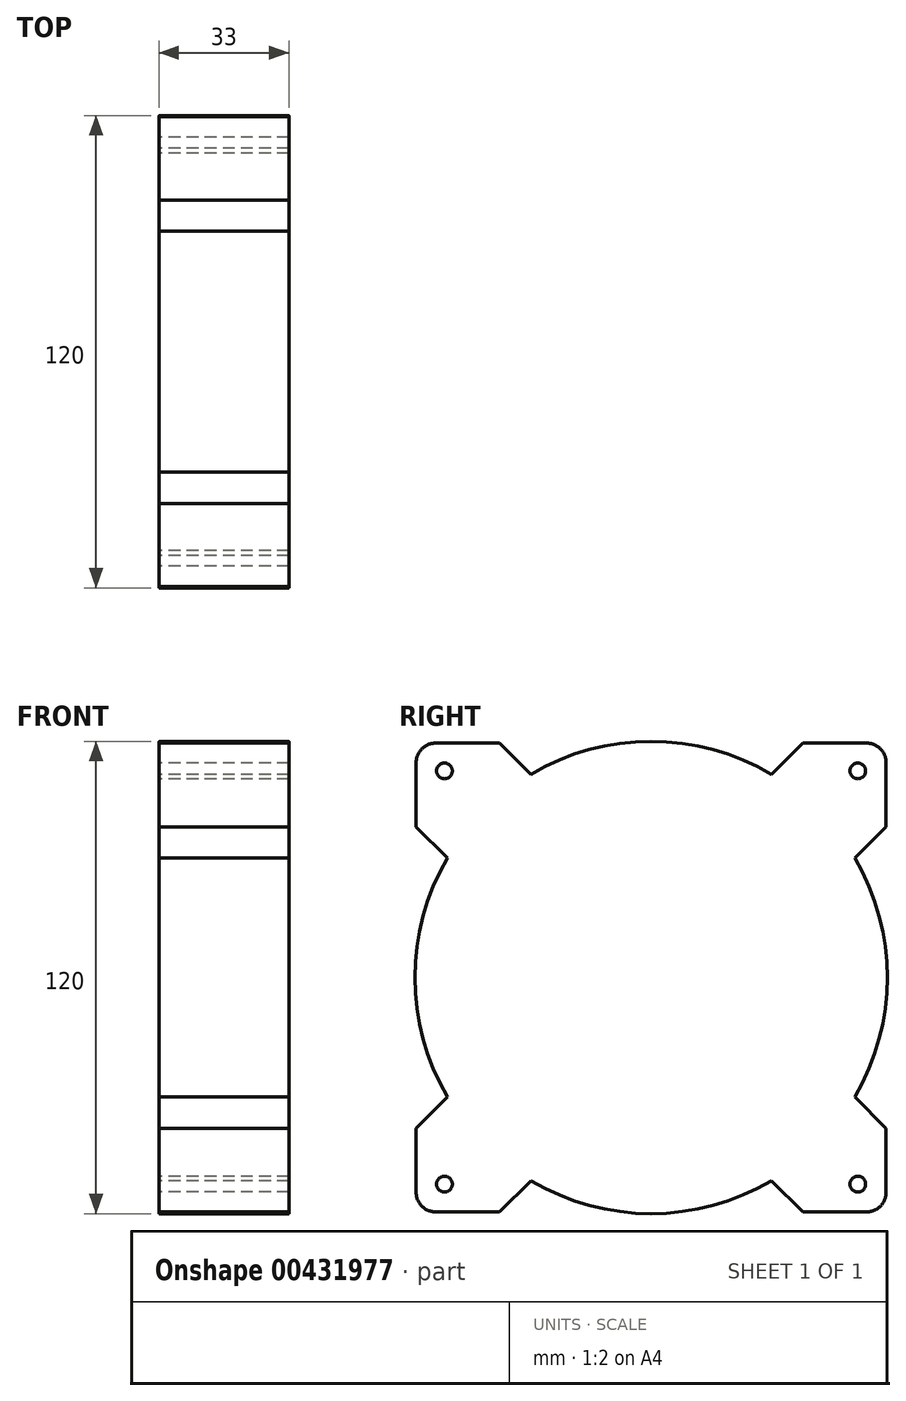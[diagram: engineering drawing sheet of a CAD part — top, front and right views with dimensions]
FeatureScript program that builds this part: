
annotation { "Feature Type Name" : "Feature", "Feature Type Description" : "" }
export const myFeature = defineFeature(function(context is Context, id is Id, definition is map)
    precondition{}
    {
        {
            var Q0;
            Q0=qCreatedBy(makeId("Right.planeOp"),FACE);
            var sketch = newSketch(context, id + "F0", { "sketchPlane" : qUnion([Q0])});
            skLineSegment(sketch, "E0.top", {"start": v(-5.3, 119.57) * mm, "end": v(-21.47, 119.57) * mm});
            skPoint(sketch, "E1.centerSnap1", {"position": v(0, 60) * mm});
            skLineSegment(sketch, "E2", {"start": v(-29.42, 111.62) * mm, "end": v(-21.47, 119.57) * mm});
            skLineSegment(sketch, "E3", {"start": v(-8.25, 90.36) * mm, "end": v(-0.3, 98.31) * mm});
            skPoint(sketch, "E4.visualSharp", {"position": v(0, 119.57) * mm});
            skArc(sketch, "E4.filletArc", {"start": v(-0.3, 114.52) * mm, "mid": v(-1.75, 118.09) * mm, "end": v(-5.3, 119.57) * mm});
            skLineSegment(sketch, "E5", {"start": v(-60, 133.31) * mm, "end": v(-60, 60) * mm, "construction": true});
            skLineSegment(sketch, "E6", {"start": v(-60, 60) * mm, "end": v(15.56, 60) * mm, "construction": true});
            skArc(sketch, "E7.trimOffspring", {"start": v(0, 60) * mm, "mid": v(-2.1, 75.73) * mm, "end": v(-8.25, 90.36) * mm});
            skLineSegment(sketch, "E8.trimOffspring", {"start": v(-0.3, 98.31) * mm, "end": v(-0.3, 114.52) * mm});
            skArc(sketch, "E9.trimOffspring", {"start": v(-29.42, 111.62) * mm, "mid": v(-44.15, 117.87) * mm, "end": v(-60, 120) * mm});
            skCircle(sketch, "E10", {"center": v(-7.5, 112.5) * mm, "radius": 2 * mm});
            skArc(sketch, "E11.MirrorCS", {"start": v(-119.7, 114.52) * mm, "mid": v(-118.25, 118.09) * mm, "end": v(-114.7, 119.57) * mm});
            skLineSegment(sketch, "E12.MirrorCS", {"start": v(-119.7, 98.31) * mm, "end": v(-119.7, 114.52) * mm});
            skArc(sketch, "E13.MirrorCS", {"start": v(-90.58, 111.62) * mm, "mid": v(-75.85, 117.87) * mm, "end": v(-60, 120) * mm});
            skCircle(sketch, "E14.MirrorC", {"center": v(-112.5, 112.5) * mm, "radius": 2 * mm});
            skPoint(sketch, "E15.MirrorP", {"position": v(-120, 119.57) * mm});
            skLineSegment(sketch, "E16.MirrorCS", {"start": v(-90.58, 111.62) * mm, "end": v(-98.53, 119.57) * mm});
            skLineSegment(sketch, "E17.MirrorCS", {"start": v(-114.7, 119.57) * mm, "end": v(-98.53, 119.57) * mm});
            skLineSegment(sketch, "E18.MirrorCS", {"start": v(-111.75, 90.36) * mm, "end": v(-119.7, 98.31) * mm});
            skArc(sketch, "E19.MirrorCS", {"start": v(-120, 60) * mm, "mid": v(-117.9, 75.73) * mm, "end": v(-111.75, 90.36) * mm});
            skArc(sketch, "E20.MirrorCS", {"start": v(-119.7, 5.48) * mm, "mid": v(-118.25, 1.91) * mm, "end": v(-114.7, 0.43) * mm});
            skArc(sketch, "E21.MirrorCS", {"start": v(-0.3, 5.48) * mm, "mid": v(-1.75, 1.91) * mm, "end": v(-5.3, 0.43) * mm});
            skLineSegment(sketch, "E22.MirrorCS", {"start": v(-111.75, 29.64) * mm, "end": v(-119.7, 21.69) * mm});
            skCircle(sketch, "E23.MirrorC", {"center": v(-7.5, 7.5) * mm, "radius": 2 * mm});
            skArc(sketch, "E24.MirrorCS", {"start": v(-90.58, 8.38) * mm, "mid": v(-75.85, 2.13) * mm, "end": v(-60, 0) * mm});
            skLineSegment(sketch, "E25.MirrorCS", {"start": v(-119.7, 21.69) * mm, "end": v(-119.7, 5.48) * mm});
            skArc(sketch, "E26.MirrorCS", {"start": v(-120, 60) * mm, "mid": v(-117.9, 44.27) * mm, "end": v(-111.75, 29.64) * mm});
            skCircle(sketch, "E27.MirrorC", {"center": v(-112.5, 7.5) * mm, "radius": 2 * mm});
            skPoint(sketch, "E28.MirrorP", {"position": v(-120, 0.43) * mm});
            skLineSegment(sketch, "E29.MirrorCS", {"start": v(-90.58, 8.38) * mm, "end": v(-98.53, 0.43) * mm});
            skPoint(sketch, "E30.MirrorP", {"position": v(0, 0.43) * mm});
            skArc(sketch, "E31.MirrorCS", {"start": v(0, 60) * mm, "mid": v(-2.1, 44.27) * mm, "end": v(-8.25, 29.64) * mm});
            skLineSegment(sketch, "E32.MirrorCS", {"start": v(-0.3, 21.69) * mm, "end": v(-0.3, 5.48) * mm});
            skLineSegment(sketch, "E33.MirrorCS", {"start": v(-5.3, 0.43) * mm, "end": v(-21.47, 0.43) * mm});
            skLineSegment(sketch, "E34.MirrorCS", {"start": v(-29.42, 8.38) * mm, "end": v(-21.47, 0.43) * mm});
            skLineSegment(sketch, "E35.MirrorCS", {"start": v(-8.25, 29.64) * mm, "end": v(-0.3, 21.69) * mm});
            skLineSegment(sketch, "E36.MirrorCS", {"start": v(-114.7, 0.43) * mm, "end": v(-98.53, 0.43) * mm});
            skArc(sketch, "E37.MirrorCS", {"start": v(-29.42, 8.38) * mm, "mid": v(-44.15, 2.13) * mm, "end": v(-60, 0) * mm});
            skSolve(sketch);
        }
        {
            var Q0;
            Q0=qSketchRegion(id+"F0",true);
            extrude(context, id + "F1", {"entities" : qUnion([Q0]), "depth" : 33 * mm});
        }
        {
            var Q0;
            Q0 = qSketchRegion(id + "F0", true);
            extrude(context, id + "F2", {"entities" : qUnion([Q0]), "operationType" : NewBodyOperationType.ADD, "depth" : 26 * mm});
        }
    });
